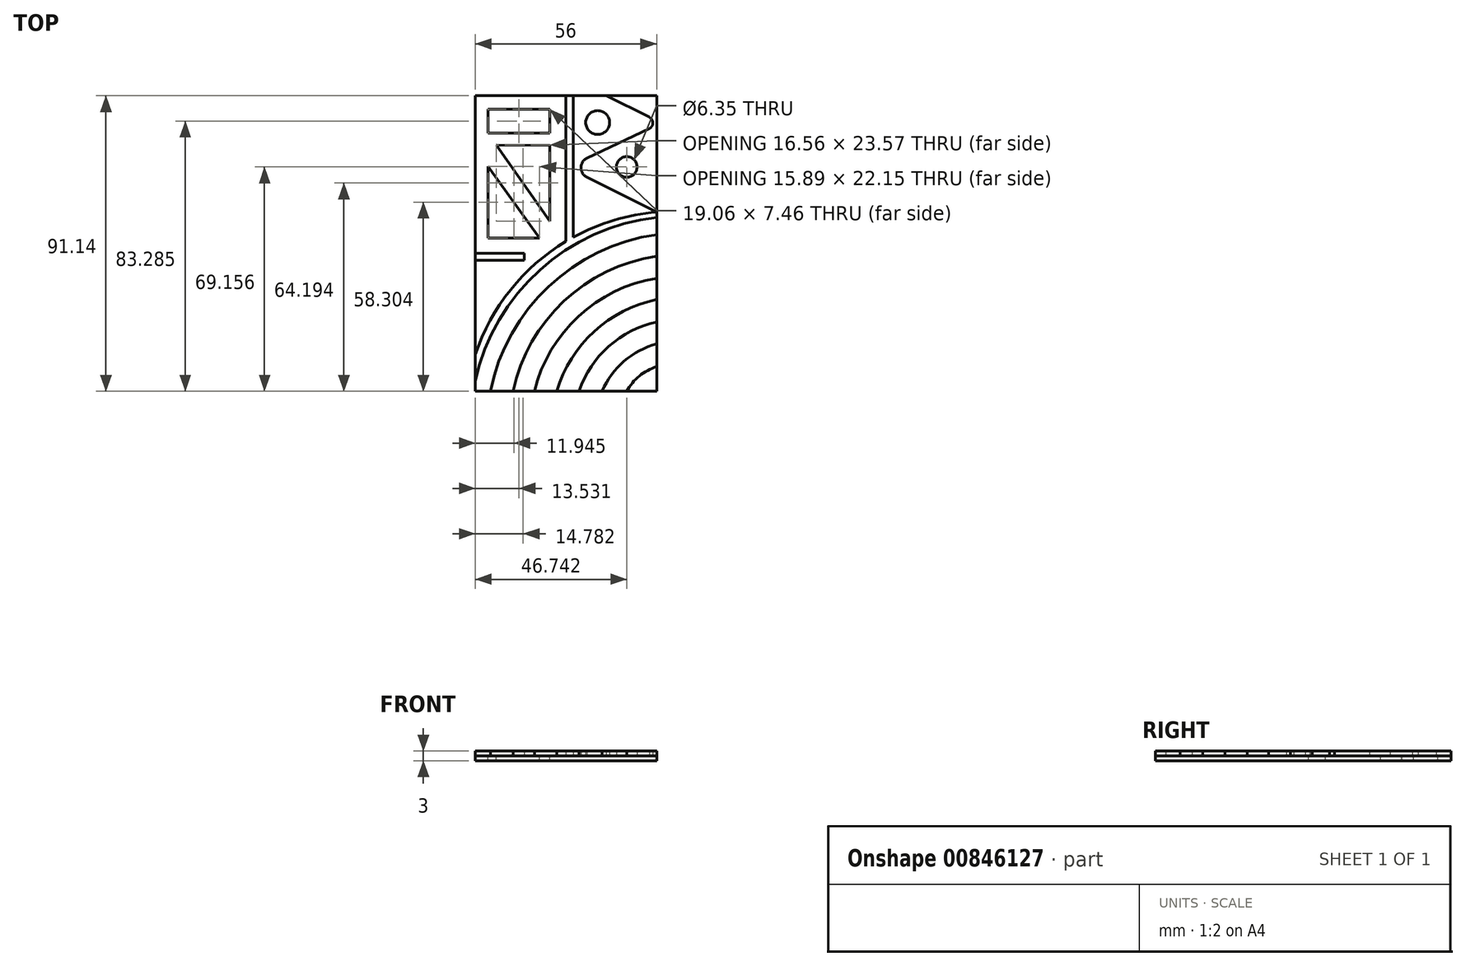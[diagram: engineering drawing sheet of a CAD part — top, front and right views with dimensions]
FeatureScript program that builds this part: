
annotation { "Feature Type Name" : "Feature", "Feature Type Description" : "" }
export const myFeature = defineFeature(function(context is Context, id is Id, definition is map)
    precondition{}
    {
        {
            var Q0;
            Q0=qCreatedBy(makeId("Top.planeOp"),FACE);
            var sketch = newSketch(context, id + "F0", { "sketchPlane" : qUnion([Q0])});
            skPoint(sketch, "E0.middle", {"position": v(-48.48, 28.7) * mm});
            skCircle(sketch, "E1", {"center": v(-23.68, 27.64) * mm, "radius": 3.67 * mm});
            skCircle(sketch, "E2", {"center": v(-14.7, 13.92) * mm, "radius": 3.18 * mm});
            skPoint(sketch, "E3.orphan", {"position": v(-57.92, 20.78) * mm});
            skArc(sketch, "E4", {"start": v(-5.45, -47.68) * mm, "mid": v(-10.8, -50.58) * mm, "end": v(-14.73, -55.24) * mm});
            skArc(sketch, "E5", {"start": v(-5.45, -40.67) * mm, "mid": v(-15.54, -46.03) * mm, "end": v(-22.28, -55.24) * mm});
            skArc(sketch, "E6", {"start": v(-5.45, -33.88) * mm, "mid": v(-20.23, -41.42) * mm, "end": v(-29.4, -55.24) * mm});
            skArc(sketch, "E7", {"start": v(-5.45, -26.99) * mm, "mid": v(-24.77, -36.86) * mm, "end": v(-36.3, -55.24) * mm});
            skArc(sketch, "E8", {"start": v(-5.45, -20.42) * mm, "mid": v(-29.58, -32.13) * mm, "end": v(-43.2, -55.24) * mm});
            skArc(sketch, "E9", {"start": v(-5.45, -13.63) * mm, "mid": v(-34.13, -27.48) * mm, "end": v(-49.76, -55.24) * mm});
            skArc(sketch, "E10", {"start": v(-5.45, -6.95) * mm, "mid": v(-38.8, -22.93) * mm, "end": v(-56.77, -55.24) * mm});
            skLineSegment(sketch, "E11", {"start": v(-5.45, -6.95) * mm, "end": v(-5.45, -13.63) * mm});
            skLineSegment(sketch, "E12", {"start": v(-5.45, -20.42) * mm, "end": v(-5.45, -26.99) * mm});
            skLineSegment(sketch, "E13", {"start": v(-5.45, -33.88) * mm, "end": v(-5.45, -40.67) * mm});
            skLineSegment(sketch, "E14", {"start": v(-5.45, -47.68) * mm, "end": v(-5.45, -55.24) * mm});
            skLineSegment(sketch, "E15", {"start": v(-5.45, -55.24) * mm, "end": v(-14.73, -55.24) * mm});
            skLineSegment(sketch, "E16", {"start": v(-22.28, -55.24) * mm, "end": v(-29.4, -55.24) * mm});
            skLineSegment(sketch, "E17", {"start": v(-36.3, -55.24) * mm, "end": v(-43.2, -55.24) * mm});
            skLineSegment(sketch, "E18", {"start": v(-49.76, -55.24) * mm, "end": v(-56.77, -55.24) * mm});
            skArc(sketch, "E19", {"start": v(-5.45, -1.61) * mm, "mid": v(-41.55, -17.89) * mm, "end": v(-61.45, -52.13) * mm});
            skArc(sketch, "E20", {"start": v(-5.45, 0) * mm, "mid": v(-18.73, -2.5) * mm, "end": v(-31.2, -7.73) * mm});
            skLineSegment(sketch, "E21", {"start": v(-5.45, -1.61) * mm, "end": v(-5.45, 0) * mm});
            skLineSegment(sketch, "E22", {"start": v(-61.45, -52.13) * mm, "end": v(-61.45, -43.94) * mm});
            skLineSegment(sketch, "E23", {"start": v(-31.2, -7.73) * mm, "end": v(-31.2, 35.9) * mm});
            skLineSegment(sketch, "E24", {"start": v(-31.2, 35.9) * mm, "end": v(-33.45, 35.9) * mm});
            skLineSegment(sketch, "E25", {"start": v(-33.45, 35.9) * mm, "end": v(-33.45, -9.02) * mm});
            skArc(sketch, "E26.trimOffspring", {"start": v(-33.45, -9.02) * mm, "mid": v(-50.57, -23.98) * mm, "end": v(-61.45, -43.94) * mm});
            skLineSegment(sketch, "E27", {"start": v(-21.08, 35.9) * mm, "end": v(-7.77, 29.29) * mm});
            skLineSegment(sketch, "E28", {"start": v(-7.77, 25.73) * mm, "end": v(-27, 16.62) * mm});
            skLineSegment(sketch, "E29", {"start": v(-27, 10.79) * mm, "end": v(-5.45, 0) * mm});
            skLineSegment(sketch, "E30", {"start": v(-5.45, 0) * mm, "end": v(-5.45, 35.9) * mm});
            skLineSegment(sketch, "E31", {"start": v(-5.45, 35.9) * mm, "end": v(-21.08, 35.9) * mm});
            skArc(sketch, "E32", {"start": v(-7.77, 29.29) * mm, "mid": v(-6.67, 27.51) * mm, "end": v(-7.77, 25.73) * mm});
            skArc(sketch, "E33", {"start": v(-27, 16.62) * mm, "mid": v(-28.85, 13.7) * mm, "end": v(-27, 10.79) * mm});
            skLineSegment(sketch, "E34.bottom", {"start": v(-61.45, -12.66) * mm, "end": v(-46.26, -12.66) * mm});
            skLineSegment(sketch, "E34.top", {"start": v(-61.45, -14.9) * mm, "end": v(-46.26, -14.9) * mm});
            skLineSegment(sketch, "E34.left", {"start": v(-61.45, -12.66) * mm, "end": v(-61.45, -14.9) * mm});
            skLineSegment(sketch, "E34.right", {"start": v(-46.26, -12.66) * mm, "end": v(-46.26, -14.9) * mm});
            skPoint(sketch, "E0.right.end.orphan", {"position": v(-57.92, 25.47) * mm});
            skPoint(sketch, "E0.bottom.end.orphan", {"position": v(-57.92, 31.9) * mm});
            skPoint(sketch, "E0.left.end.orphan", {"position": v(-39.04, 25.47) * mm});
            skPoint(sketch, "E0.left.start.orphan", {"position": v(-39.04, 31.9) * mm});
            skSolve(sketch);
        }
        {
            var Q0;
            Q0 = qSketchRegion(id + "F0", true);
            extrude(context, id + "F1", {"entities" : qUnion([Q0]), "depth" : 1.5 * mm, "offsetDistance" : 25 * mm});
        }
        {
            var Q0;
            Q0=qCreatedBy(makeId("Top.planeOp"),FACE);
            var sketch = newSketch(context, id + "F2", { "sketchPlane" : qUnion([Q0])});
            skLineSegment(sketch, "E35.0", {"start": v(-5.45, 35.9) * mm, "end": v(-61.45, 35.9) * mm});
            skLineSegment(sketch, "E36.0", {"start": v(-61.45, 35.9) * mm, "end": v(-61.45, -55.24) * mm});
            skLineSegment(sketch, "E37.0", {"start": v(-61.45, -55.24) * mm, "end": v(-5.45, -55.24) * mm});
            skLineSegment(sketch, "E38.0", {"start": v(-5.45, -55.24) * mm, "end": v(-5.45, 35.9) * mm});
            skSolve(sketch);
        }
        {
            var Q0;
            Q0=makeQuery(id+"F2.imprint","IMPRINT",FACE,{"disambiguationData":[TD([[makeQuery(id+"F2.imprint","IMPRINT",EDGE,{"derivedFrom":sQuery(id+"F2.wireOp",EDGE,"E35.0")}),1.0]])]});
            extrude(context, id + "F3", {"entities" : qUnion([Q0]), "oppositeDirection" : true, "depth" : 1.5 * mm, "offsetDistance" : 25 * mm});
        }
        {
            var Q0;
            Q0=qCreatedBy(makeId("Top.planeOp"),FACE);
            var sketch = newSketch(context, id + "F4", { "sketchPlane" : qUnion([Q0])});
            skLineSegment(sketch, "E39.bottom", {"start": v(-38.4, 31.77) * mm, "end": v(-57.45, 31.77) * mm});
            skLineSegment(sketch, "E39.top", {"start": v(-38.4, 24.32) * mm, "end": v(-57.45, 24.32) * mm});
            skLineSegment(sketch, "E39.left", {"start": v(-38.4, 31.77) * mm, "end": v(-38.4, 24.32) * mm});
            skLineSegment(sketch, "E39.right", {"start": v(-57.45, 31.77) * mm, "end": v(-57.45, 24.32) * mm});
            skPoint(sketch, "E39.middle", {"position": v(-47.92, 28.04) * mm});
            skLineSegment(sketch, "E40", {"start": v(-38.4, 20.62) * mm, "end": v(-38.4, -2.83) * mm});
            skLineSegment(sketch, "E41", {"start": v(-38.4, -2.83) * mm, "end": v(-54.95, 20.74) * mm});
            skLineSegment(sketch, "E42", {"start": v(-54.95, 20.74) * mm, "end": v(-38.4, 20.62) * mm});
            skLineSegment(sketch, "E43", {"start": v(-57.45, 14.14) * mm, "end": v(-57.45, -8) * mm});
            skLineSegment(sketch, "E44", {"start": v(-57.45, -8) * mm, "end": v(-41.56, -8) * mm});
            skLineSegment(sketch, "E45", {"start": v(-41.56, -8) * mm, "end": v(-57.45, 14.14) * mm});
            skSolve(sketch);
        }
        {
            var Q0;
            Q0 = qSketchRegion(id + "F4", true);
            extrude(context, id + "F5", {"entities" : qUnion([Q0]), "operationType" : NewBodyOperationType.REMOVE, "oppositeDirection" : true, "depth" : 25 * mm, "offsetDistance" : 25 * mm});
        }
    });
